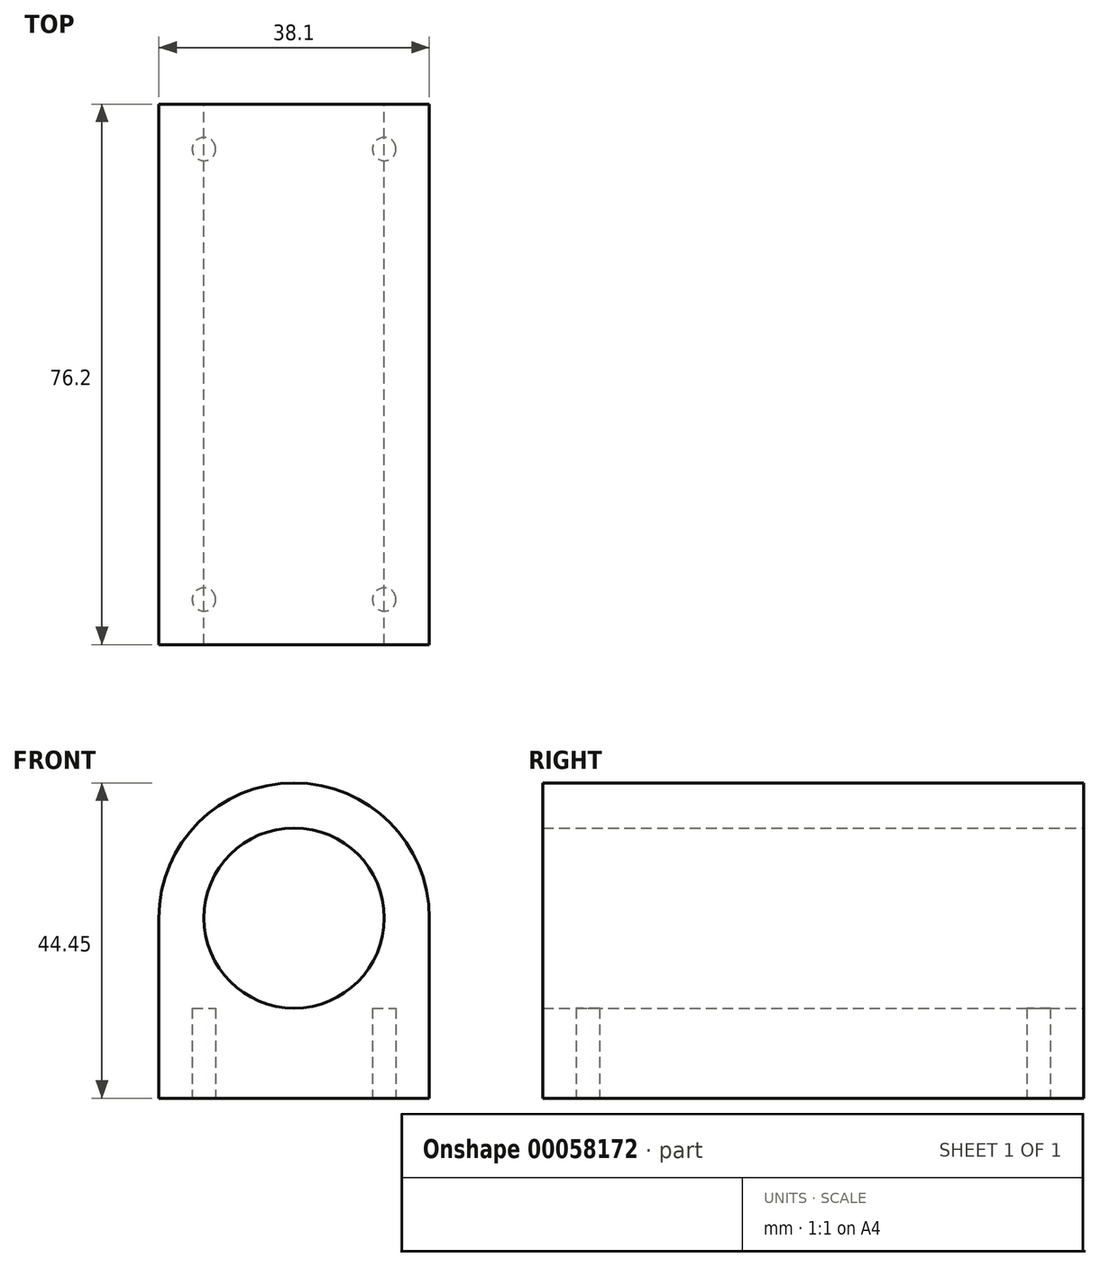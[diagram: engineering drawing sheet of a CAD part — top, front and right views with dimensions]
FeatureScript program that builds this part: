
annotation { "Feature Type Name" : "Feature", "Feature Type Description" : "" }
export const myFeature = defineFeature(function(context is Context, id is Id, definition is map)
    precondition{}
    {
        {
            var Q0;
            Q0=qCreatedBy(makeId("Front.planeOp"),FACE);
            var sketch = newSketch(context, id + "F0", { "sketchPlane" : qUnion([Q0])});
            skCircle(sketch, "E0", {"center": v(0, 0) * mm, "radius": 12.7 * mm});
            skArc(sketch, "E1", {"start": v(19.05, 0) * mm, "mid": v(0, 19.05) * mm, "end": v(-19.05, 0) * mm});
            skLineSegment(sketch, "E2", {"start": v(-19.05, 0) * mm, "end": v(-19.05, -25.4) * mm});
            skLineSegment(sketch, "E3", {"start": v(-19.05, -25.4) * mm, "end": v(19.05, -25.4) * mm});
            skLineSegment(sketch, "E4", {"start": v(19.05, -25.4) * mm, "end": v(19.05, 0) * mm});
            skSolve(sketch);
        }
        {
            var Q0;
            Q0=makeQuery(id+"F0.imprint","IMPRINT",FACE,{"disambiguationData":[TD([[makeQuery(id+"F0.imprint","IMPRINT",EDGE,{"derivedFrom":sQuery(id+"F0.wireOp",EDGE,"E0")}),-1.0]])]});
            extrude(context, id + "F1", {"entities" : qUnion([Q0]), "depth" : 76.2 * mm});
        }
        {
            var Q0;
            Q0=makeQuery(id+"F1.opExtrude","SWEPT_FACE",FACE,{"disambiguationData":[OSD([sQuery(id+"F0.wireOp",EDGE,"E3")])]});
            var sketch = newSketch(context, id + "F2", { "sketchPlane" : qUnion([Q0])});
            skCircle(sketch, "E5", {"center": v(-12.7, 69.85) * mm, "radius": 1.65 * mm});
            skCircle(sketch, "E6", {"center": v(-12.7, 6.35) * mm, "radius": 1.65 * mm});
            skPoint(sketch, "E7.startSnap0", {"position": v(0, 76.2) * mm});
            skCircle(sketch, "E8", {"center": v(12.7, 69.85) * mm, "radius": 1.65 * mm});
            skCircle(sketch, "E9", {"center": v(12.7, 6.35) * mm, "radius": 1.65 * mm});
            skSolve(sketch);
        }
        {
            var Q0;
            Q0=makeQuery(id+"F2.imprint","IMPRINT",FACE,{"disambiguationData":[TD([[makeQuery(id+"F2.imprint","IMPRINT",EDGE,{"derivedFrom":sQuery(id+"F2.wireOp",EDGE,"E5")}),1.0]])]});
            var Q1;
            Q1=makeQuery(id+"F2.imprint","IMPRINT",FACE,{"disambiguationData":[TD([[makeQuery(id+"F2.imprint","IMPRINT",EDGE,{"derivedFrom":sQuery(id+"F2.wireOp",EDGE,"E8")}),1.0]])]});
            var Q2;
            Q2=makeQuery(id+"F2.imprint","IMPRINT",FACE,{"disambiguationData":[TD([[makeQuery(id+"F2.imprint","IMPRINT",EDGE,{"derivedFrom":sQuery(id+"F2.wireOp",EDGE,"E6")}),1.0]])]});
            var Q3;
            Q3=makeQuery(id+"F2.imprint","IMPRINT",FACE,{"disambiguationData":[TD([[makeQuery(id+"F2.imprint","IMPRINT",EDGE,{"derivedFrom":sQuery(id+"F2.wireOp",EDGE,"E9")}),1.0]])]});
            extrude(context, id + "F3", {"entities" : qUnion([Q0, Q1, Q2, Q3]), "operationType" : NewBodyOperationType.REMOVE, "oppositeDirection" : true, "depth" : 12.7 * mm});
        }
    });
